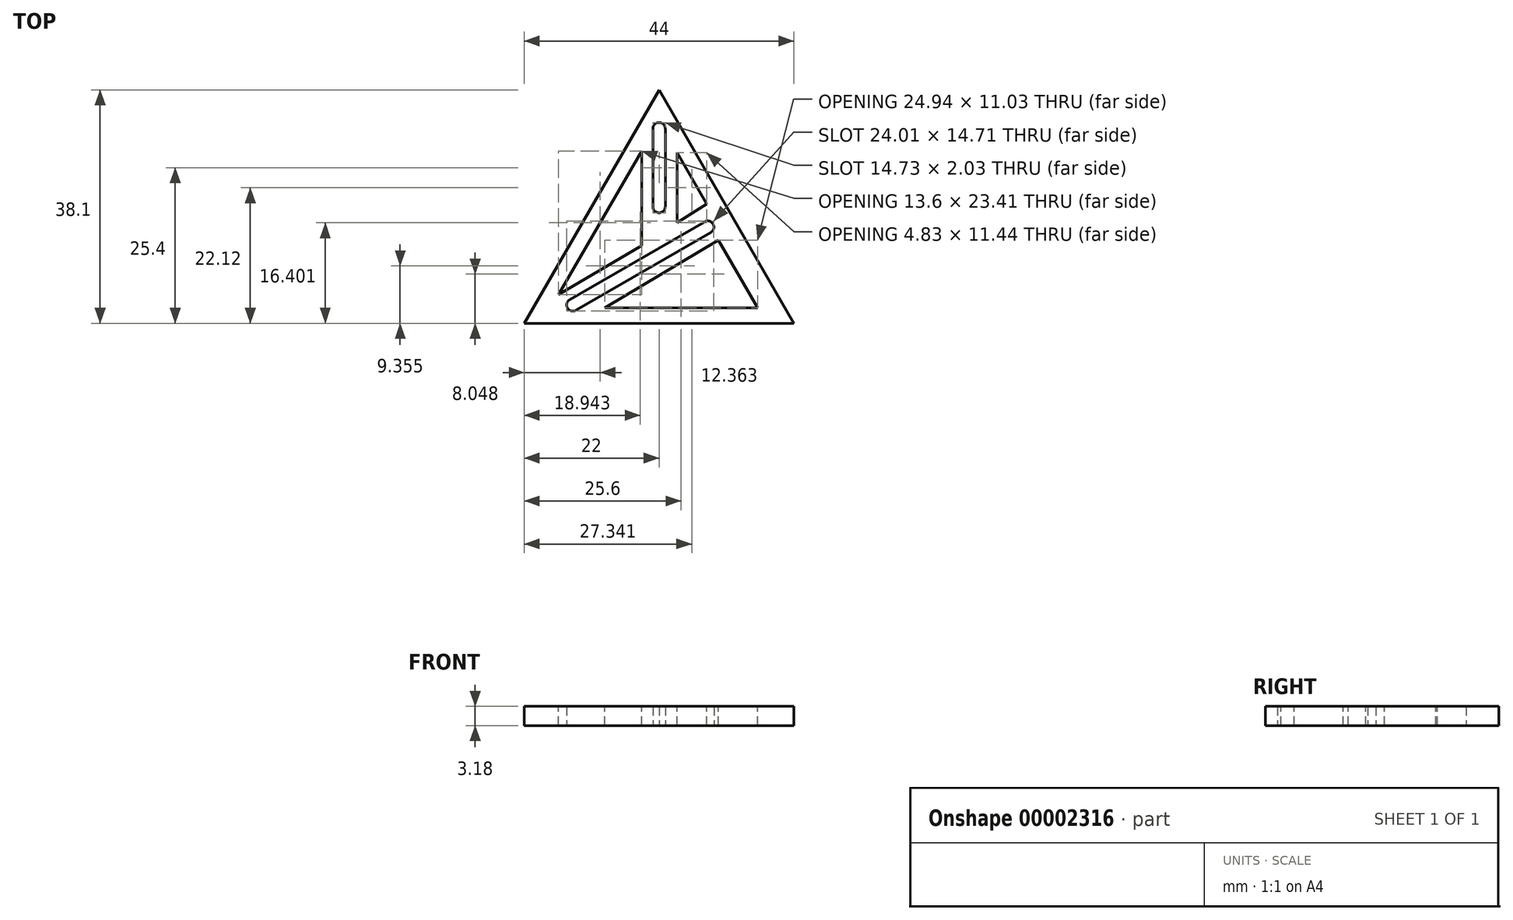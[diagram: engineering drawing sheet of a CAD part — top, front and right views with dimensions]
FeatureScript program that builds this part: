
annotation { "Feature Type Name" : "Feature", "Feature Type Description" : "" }
export const myFeature = defineFeature(function(context is Context, id is Id, definition is map)
    precondition{}
    {
        {
            var Q0;
            Q0=qCreatedBy(makeId("Top.planeOp"),FACE);
            var sketch = newSketch(context, id + "F0", { "sketchPlane" : qUnion([Q0])});
            skCircle(sketch, "E0.cCircle", {"center": v(0, 0) * mm, "radius": 12.7 * mm, "construction": true});
            skLineSegment(sketch, "E0.0", {"start": v(0, 25.4) * mm, "end": v(22, -12.7) * mm});
            skLineSegment(sketch, "E0.1", {"start": v(22, -12.7) * mm, "end": v(-22, -12.7) * mm});
            skLineSegment(sketch, "E0.2", {"start": v(-22, -12.7) * mm, "end": v(0, 25.4) * mm});
            skPoint(sketch, "E0.0.midPoint", {"position": v(11, 6.35) * mm});
            skPoint(sketch, "E1", {"position": v(0, 25.4) * mm});
            skSolve(sketch);
        }
        {
            var Q0;
            Q0=makeQuery(id+"F0.imprint","IMPRINT",FACE,{"disambiguationData":[TD([[makeQuery(id+"F0.imprint","IMPRINT",EDGE,{"derivedFrom":sQuery(id+"F0.wireOp",EDGE,"E0.0")}),-1.0]])]});
            extrude(context, id + "F1", {"entities" : qUnion([Q0]), "depth" : 3.17 * mm});
        }
        {
            var Q0;
            Q0=makeQuery(id+"F1.opExtrude","CAP_FACE",FACE,{"disambiguationData":[OSD([sQuery(id+"F0.wireOp",EDGE,"E0.0"),sQuery(id+"F0.wireOp",EDGE,"E0.1"),sQuery(id+"F0.wireOp",EDGE,"E0.2")])],"isStart":true});
            var sketch = newSketch(context, id + "F2", { "sketchPlane" : qUnion([Q0])});
            skLineSegment(sketch, "E2", {"start": v(0, 17.45) * mm, "end": v(0, -34.05) * mm});
            skSolve(sketch);
        }
        {
            var Q0;
            {var subQ3=makeQuery(id+"F1.opExtrude","CAP_EDGE",EDGE,{"disambiguationData":[OSD([sQuery(id+"F0.wireOp",EDGE,"E0.0")])],"isStart":true});Q0=makeQuery(id+"F2.imprint","IMPRINT",FACE,{"disambiguationData":[TD([[makeQuery(id+"F2.imprint","IMPRINT",EDGE,{"derivedFrom":subQ3}),1.0]])]});}
            var sketch = newSketch(context, id + "F3", { "sketchPlane" : qUnion([Q0])});
            skLineSegment(sketch, "E3.rect.left", {"start": v(1.02, -6.35) * mm, "end": v(1.02, -19.05) * mm});
            skLineSegment(sketch, "E3.rect.right", {"start": v(-1.02, -6.35) * mm, "end": v(-1.02, -19.05) * mm});
            skPoint(sketch, "E3.rect.middle", {"position": v(0, -12.7) * mm});
            skArc(sketch, "E4", {"start": v(-1.02, -6.35) * mm, "mid": v(0, -5.33) * mm, "end": v(1.02, -6.35) * mm});
            skArc(sketch, "E5", {"start": v(-1.02, -19.05) * mm, "mid": v(0, -20.07) * mm, "end": v(1.02, -19.05) * mm});
            skSolve(sketch);
        }
        {
            var Q0;
            {var subQ7=sQuery(id+"F3.wireOp",EDGE,"E3.rect.right");var subQ8=sQuery(id+"F3.wireOp",EDGE,"E3.rect.left");Q0=qUnion([makeQuery(id+"F3.imprint","IMPRINT",FACE,{"disambiguationData":[TD([[makeQuery(id+"F3.imprint","IMPRINT",EDGE,{"derivedFrom":subQ7}),1.0]])]}),makeQuery(id+"F3.imprint","IMPRINT",FACE,{"disambiguationData":[TD([[makeQuery(id+"F3.imprint","IMPRINT",EDGE,{"derivedFrom":subQ8}),-1.0]])]})]);}
            extrude(context, id + "F4", {"entities" : qUnion([Q0]), "operationType" : NewBodyOperationType.REMOVE, "oppositeDirection" : true, "depth" : 6.6 * mm});
        }
        {
            var Q0;
            {var subQ3=makeQuery(id+"F1.opExtrude","CAP_EDGE",EDGE,{"disambiguationData":[OSD([sQuery(id+"F0.wireOp",EDGE,"E0.2")])],"isStart":true});Q0=makeQuery(id+"F2.imprint","IMPRINT",FACE,{"disambiguationData":[TD([[makeQuery(id+"F2.imprint","IMPRINT",EDGE,{"derivedFrom":subQ3}),1.0]])]});}
            var sketch = newSketch(context, id + "F5", { "sketchPlane" : qUnion([Q0])});
            skPoint(sketch, "E6", {"position": v(-14.56, 8.81) * mm});
            skPoint(sketch, "E7", {"position": v(7.43, -3.89) * mm});
            skLineSegment(sketch, "E8", {"start": v(-14.56, 8.81) * mm, "end": v(7.43, -3.89) * mm});
            skLineSegment(sketch, "E9", {"start": v(-13.55, 10.57) * mm, "end": v(8.45, -2.13) * mm});
            skArc(sketch, "E10", {"start": v(-14.56, 8.81) * mm, "mid": v(-14.94, 10.2) * mm, "end": v(-13.55, 10.57) * mm});
            skArc(sketch, "E11", {"start": v(8.45, -2.13) * mm, "mid": v(8.82, -3.51) * mm, "end": v(7.43, -3.89) * mm});
            skLineSegment(sketch, "E12", {"start": v(-14.06, 9.7) * mm, "end": v(7.94, -3) * mm});
            skSolve(sketch);
        }
        {
            var Q0;
            Q0 = qSketchRegion(id + "F5", true);
            extrude(context, id + "F6", {"entities" : qUnion([Q0]), "operationType" : NewBodyOperationType.REMOVE, "oppositeDirection" : true, "depth" : 6.35 * mm});
        }
        {
            var Q0;
            Q0=makeQuery(id+"F1.opExtrude","CAP_FACE",FACE,{"disambiguationData":[OSD([sQuery(id+"F0.wireOp",EDGE,"E0.0"),sQuery(id+"F0.wireOp",EDGE,"E0.1"),sQuery(id+"F0.wireOp",EDGE,"E0.2")])],"isStart":false});
            var sketch = newSketch(context, id + "F7", { "sketchPlane" : qUnion([Q0])});
            skLineSegment(sketch, "E13", {"start": v(-2.84, 15.4) * mm, "end": v(-2.84, 0) * mm});
            skLineSegment(sketch, "E14", {"start": v(-2.84, 0) * mm, "end": v(-16.44, -8) * mm});
            skLineSegment(sketch, "E15", {"start": v(-16.44, -8) * mm, "end": v(-2.84, 15.4) * mm});
            skLineSegment(sketch, "E16", {"start": v(9.7, 0.86) * mm, "end": v(-8.87, -10.17) * mm});
            skLineSegment(sketch, "E17", {"start": v(-8.87, -10.17) * mm, "end": v(16.07, -10.17) * mm});
            skLineSegment(sketch, "E18", {"start": v(16.07, -10.17) * mm, "end": v(9.7, 0.86) * mm});
            skLineSegment(sketch, "E19", {"start": v(2.92, 3.7) * mm, "end": v(2.92, 15.14) * mm});
            skLineSegment(sketch, "E20", {"start": v(2.92, 15.14) * mm, "end": v(7.76, 6.77) * mm});
            skLineSegment(sketch, "E21", {"start": v(7.76, 6.77) * mm, "end": v(2.92, 3.7) * mm});
            skSolve(sketch);
        }
        {
            var Q0;
            {Q0=qUnion([makeQuery(id+"F7.imprint","IMPRINT",FACE,{"disambiguationData":[TD([[makeQuery(id+"F7.imprint","IMPRINT",EDGE,{"derivedFrom":sQuery(id+"F7.wireOp",EDGE,"E13")}),-1.0]])]}),makeQuery(id+"F7.imprint","IMPRINT",FACE,{"disambiguationData":[TD([[makeQuery(id+"F7.imprint","IMPRINT",EDGE,{"derivedFrom":sQuery(id+"F7.wireOp",EDGE,"E16")}),1.0]])]}),makeQuery(id+"F7.imprint","IMPRINT",FACE,{"disambiguationData":[TD([[makeQuery(id+"F7.imprint","IMPRINT",EDGE,{"derivedFrom":sQuery(id+"F7.wireOp",EDGE,"E19")}),-1.0]])]})]);}
            extrude(context, id + "F8", {"entities" : qUnion([Q0]), "operationType" : NewBodyOperationType.REMOVE, "oppositeDirection" : true, "depth" : 25.4 * mm});
        }
    });
